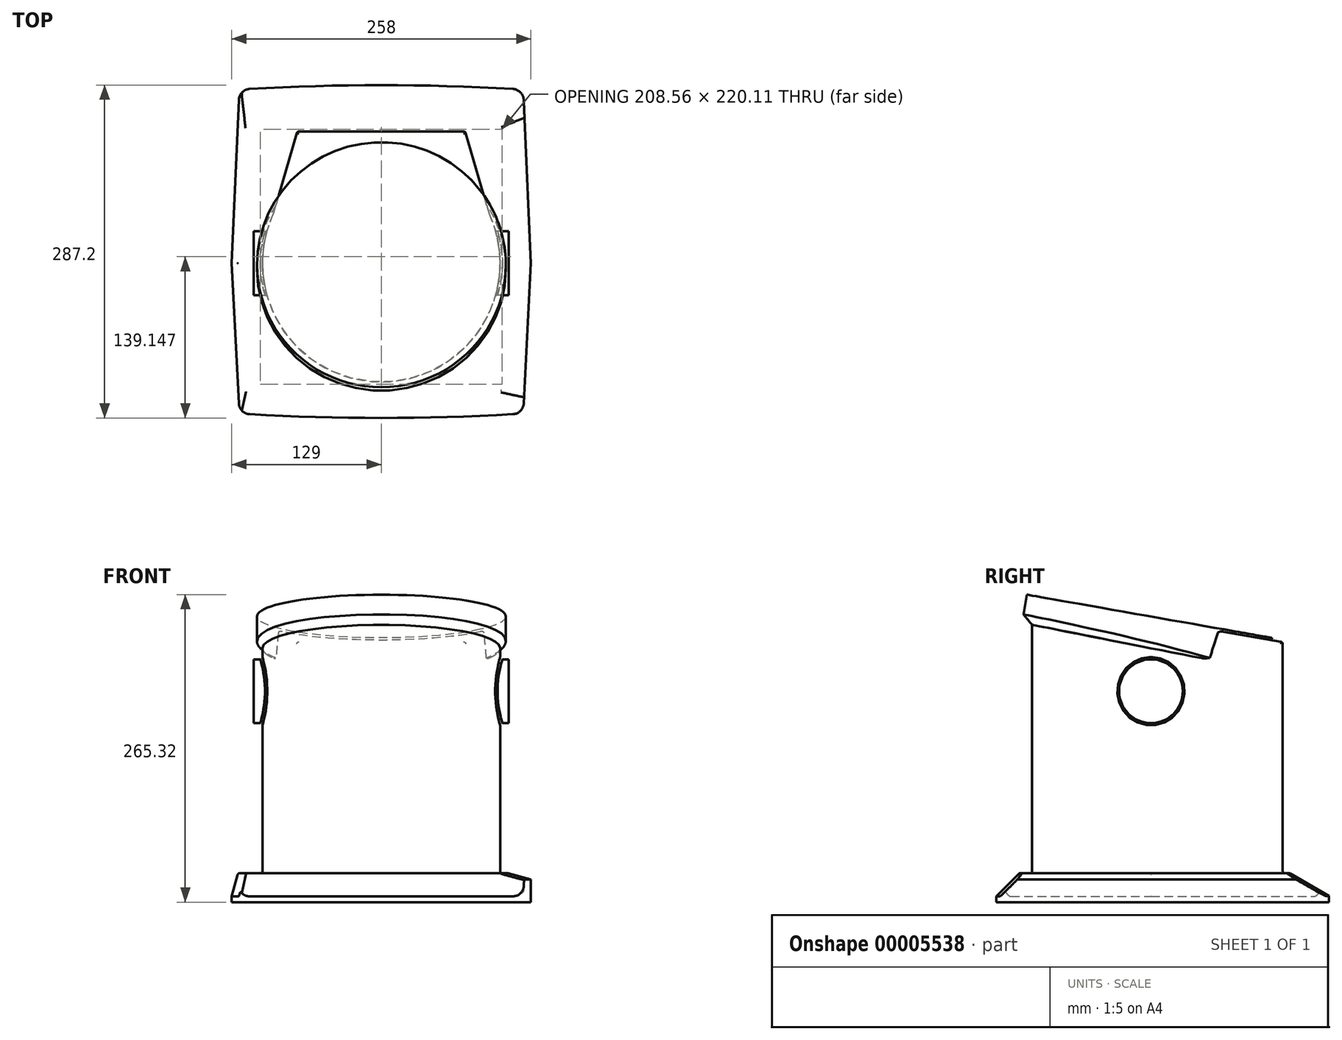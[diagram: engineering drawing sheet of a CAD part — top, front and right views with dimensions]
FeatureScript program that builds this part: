
annotation { "Feature Type Name" : "Feature", "Feature Type Description" : "" }
export const myFeature = defineFeature(function(context is Context, id is Id, definition is map)
    precondition{}
    {
        {
            var Q0;
            Q0=qCreatedBy(makeId("Top.planeOp"),FACE);
            var sketch = newSketch(context, id + "F0", { "sketchPlane" : qUnion([Q0])});
            skLineSegment(sketch, "E0", {"start": v(-129, 0) * mm, "end": v(-122.5, 149.86) * mm});
            skLineSegment(sketch, "E1", {"start": v(-122.5, 149.86) * mm, "end": v(122.5, 149.86) * mm, "construction": true});
            skLineSegment(sketch, "E2", {"start": v(122.5, 149.86) * mm, "end": v(129, 0) * mm});
            skLineSegment(sketch, "E3", {"start": v(129, 0) * mm, "end": v(122.5, -129.84) * mm});
            skLineSegment(sketch, "E4", {"start": v(122.5, -129.84) * mm, "end": v(-122.5, -129.84) * mm, "construction": true});
            skLineSegment(sketch, "E5", {"start": v(-122.5, -129.84) * mm, "end": v(-129, 0) * mm});
            skArc(sketch, "E6", {"start": v(122.5, 149.86) * mm, "mid": v(0, 153.61) * mm, "end": v(-122.5, 149.86) * mm});
            skArc(sketch, "E7", {"start": v(-122.5, -129.84) * mm, "mid": v(0, -133.6) * mm, "end": v(122.5, -129.84) * mm});
            skLineSegment(sketch, "E8", {"start": v(-129, 0) * mm, "end": v(129, 0) * mm, "construction": true});
            skPoint(sketch, "E9", {"position": v(0, 0) * mm});
            skPoint(sketch, "E10", {"position": v(0, 149.86) * mm});
            skPoint(sketch, "E11", {"position": v(0, -129.84) * mm});
            skSolve(sketch);
        }
        {
            var Q0;
            Q0=makeQuery(id+"F0.imprint","IMPRINT",FACE,{"disambiguationData":[TD([[makeQuery(id+"F0.imprint","IMPRINT",EDGE,{"derivedFrom":sQuery(id+"F0.wireOp",EDGE,"E0")}),-1.0]])]});
            extrude(context, id + "F1", {"entities" : qUnion([Q0]), "depth" : 25 * mm});
        }
        {
            var Q0;
            Q0=makeQuery(id+"F1.opExtrude","CAP_EDGE",EDGE,{"disambiguationData":[OSD([sQuery(id+"F0.wireOp",EDGE,"E0")])],"isStart":false});
            var Q1;
            Q1=makeQuery(id+"F1.opExtrude","CAP_EDGE",EDGE,{"disambiguationData":[OSD([sQuery(id+"F0.wireOp",EDGE,"E5")])],"isStart":false});
            var Q2;
            Q2=makeQuery(id+"F1.opExtrude","CAP_EDGE",EDGE,{"disambiguationData":[OSD([sQuery(id+"F0.wireOp",EDGE,"E3")])],"isStart":false});
            var Q3;
            Q3=makeQuery(id+"F1.opExtrude","CAP_EDGE",EDGE,{"disambiguationData":[OSD([sQuery(id+"F0.wireOp",EDGE,"E2")])],"isStart":false});
            chamfer(context, id + "F2", {"entities" : qUnion([Q0, Q1, Q2, Q3]), "chamferType" : ChamferType.OFFSET_ANGLE, "width" : 20 * mm, "oppositeDirection" : false, "angle" : 15 * degree, "tangentPropagation" : true});
        }
        {
            var Q0;
            Q0=makeQuery(id+"F1.opExtrude","CAP_EDGE",EDGE,{"disambiguationData":[OSD([sQuery(id+"F0.wireOp",EDGE,"E7")])],"isStart":false});
            chamfer(context, id + "F3", {"entities" : qUnion([Q0]), "chamferType" : ChamferType.OFFSET_ANGLE, "width" : 20 * mm, "oppositeDirection" : false, "angle" : 45 * degree, "tangentPropagation" : true});
        }
        {
            var Q0;
            Q0=makeQuery(id+"F1.opExtrude","CAP_EDGE",EDGE,{"disambiguationData":[OSD([sQuery(id+"F0.wireOp",EDGE,"E6")])],"isStart":false});
            chamfer(context, id + "F4", {"entities" : qUnion([Q0]), "chamferType" : ChamferType.OFFSET_ANGLE, "width" : 34 * mm, "oppositeDirection" : false, "angle" : 30 * degree, "tangentPropagation" : true});
        }
        {
            var Q0;
            Q0=makeQuery(id+"F1.opExtrude","CAP_FACE",FACE,{"disambiguationData":[OSD([sQuery(id+"F0.wireOp",EDGE,"E0"),sQuery(id+"F0.wireOp",EDGE,"E2"),sQuery(id+"F0.wireOp",EDGE,"E3"),sQuery(id+"F0.wireOp",EDGE,"E5"),sQuery(id+"F0.wireOp",EDGE,"E6"),sQuery(id+"F0.wireOp",EDGE,"E7")])],"isStart":false});
            var sketch = newSketch(context, id + "F5", { "sketchPlane" : qUnion([Q0])});
            skArc(sketch, "E12", {"start": v(-92.81, 43.5) * mm, "mid": v(0, -102.5) * mm, "end": v(92.81, 43.5) * mm});
            skLineSegment(sketch, "E13", {"start": v(-92.81, 43.5) * mm, "end": v(-72.5, 113.61) * mm});
            skLineSegment(sketch, "E14", {"start": v(-72.5, 113.61) * mm, "end": v(72.5, 113.61) * mm});
            skLineSegment(sketch, "E15", {"start": v(72.5, 113.61) * mm, "end": v(92.81, 43.5) * mm});
            skPoint(sketch, "E16", {"position": v(0, 113.61) * mm});
            skSolve(sketch);
        }
        {
            var Q0;
            Q0=makeQuery(id+"F5.imprint","IMPRINT",FACE,{"disambiguationData":[TD([[makeQuery(id+"F5.imprint","IMPRINT",EDGE,{"derivedFrom":sQuery(id+"F5.wireOp",EDGE,"E12")}),1.0]])]});
            extrude(context, id + "F6", {"entities" : qUnion([Q0]), "operationType" : NewBodyOperationType.ADD, "depth" : 240 * mm});
        }
        {
            var Q0;
            Q0=makeQuery(id+"F6.opExtrude","CAP_EDGE",EDGE,{"disambiguationData":[OSD([sQuery(id+"F5.wireOp",EDGE,"E14")])],"isStart":false});
            cPlane(context, id + "F7", {"entities" : qUnion([Q0]), "cplaneType" : CPlaneType.LINE_ANGLE, "offset" : 150 * mm, "angle" : 80 * degree, "width" : 150 * mm, "height" : 150 * mm});
        }
        {
            var Q0;
            Q0=qCreatedBy(id+"F7.planeOp",FACE);
            var sketch = newSketch(context, id + "F8", { "sketchPlane" : qUnion([Q0])});
            skCircle(sketch, "E17", {"center": v(0, -11.31) * mm, "radius": 170.12 * mm});
            skSolve(sketch);
        }
        {
            var Q0;
            Q0=makeQuery(id+"F8.imprint","IMPRINT",FACE,{"disambiguationData":[TD([[makeQuery(id+"F8.imprint","IMPRINT",EDGE,{"derivedFrom":sQuery(id+"F8.wireOp",EDGE,"E17")}),1.0]])]});
            extrude(context, id + "F9", {"entities" : qUnion([Q0]), "operationType" : NewBodyOperationType.REMOVE, "oppositeDirection" : true, "depth" : 40 * mm});
        }
        {
            var Q0;
            Q0=makeQuery(id+"F9.boolean.opBoolean","COPY",FACE,{"derivedFrom":makeQuery(id+"F9.opExtrude","CAP_FACE",FACE,{"disambiguationData":[OSD([sQuery(id+"F8.wireOp",EDGE,"E17")])],"isStart":false})});
            var sketch = newSketch(context, id + "F10", { "sketchPlane" : qUnion([Q0])});
            skCircle(sketch, "E18", {"center": v(0.1, -44.14) * mm, "radius": 102.33 * mm, "construction": true});
            skPoint(sketch, "E18.first.point", {"position": v(-100.45, -63.15) * mm});
            skPoint(sketch, "E18.second.point", {"position": v(21.64, -144.18) * mm});
            skPoint(sketch, "E18.third.point", {"position": v(102.35, -48.13) * mm});
            skCircle(sketch, "E19.0", {"center": v(0.1, -44.14) * mm, "radius": 107.33 * mm});
            skSolve(sketch);
        }
        {
            var Q0;
            Q0=qCreatedBy(makeId("Right.planeOp"),FACE);
            var sketch = newSketch(context, id + "F11", { "sketchPlane" : qUnion([Q0])});
            skCircle(sketch, "E20", {"center": v(0, 182) * mm, "radius": 27.5 * mm});
            skSolve(sketch);
        }
        {
            var Q0;
            Q0=makeQuery(id+"F11.imprint","IMPRINT",FACE,{"disambiguationData":[TD([[makeQuery(id+"F11.imprint","IMPRINT",EDGE,{"derivedFrom":sQuery(id+"F11.wireOp",EDGE,"E20")}),1.0]])]});
            extrude(context, id + "F12", {"entities" : qUnion([Q0]), "operationType" : NewBodyOperationType.ADD, "depth" : 110 * mm});
        }
        {
            var Q0;
            Q0=makeQuery(id+"F11.imprint","IMPRINT",FACE,{"disambiguationData":[TD([[makeQuery(id+"F11.imprint","IMPRINT",EDGE,{"derivedFrom":sQuery(id+"F11.wireOp",EDGE,"E20")}),1.0]])]});
            extrude(context, id + "F13", {"entities" : qUnion([Q0]), "operationType" : NewBodyOperationType.ADD, "oppositeDirection" : true, "depth" : 110 * mm});
        }
        {
            var Q0;
            Q0=makeQuery(id+"F1.opExtrude","CAP_FACE",FACE,{"disambiguationData":[OSD([sQuery(id+"F0.wireOp",EDGE,"E0"),sQuery(id+"F0.wireOp",EDGE,"E2"),sQuery(id+"F0.wireOp",EDGE,"E3"),sQuery(id+"F0.wireOp",EDGE,"E5"),sQuery(id+"F0.wireOp",EDGE,"E6"),sQuery(id+"F0.wireOp",EDGE,"E7")])],"isStart":false});
            var Q1;
            Q1=makeQuery(id+"F6.opExtrude","SWEPT_FACE",FACE,{"disambiguationData":[OSD([sQuery(id+"F5.wireOp",EDGE,"E14")])]});
            var Q2;
            Q2=makeQuery(id+"F6.opExtrude","SWEPT_FACE",FACE,{"disambiguationData":[OSD([sQuery(id+"F5.wireOp",EDGE,"E13")])]});
            var Q3;
            Q3=makeQuery(id+"F6.opExtrude","SWEPT_FACE",FACE,{"disambiguationData":[OSD([sQuery(id+"F5.wireOp",EDGE,"E12")])]});
            var Q4;
            Q4=makeQuery(id+"F9.boolean.opBoolean","COPY",FACE,{"derivedFrom":makeQuery(id+"F9.opExtrude","CAP_FACE",FACE,{"disambiguationData":[OSD([sQuery(id+"F8.wireOp",EDGE,"E17")])],"isStart":false})});
            var Q5;
            Q5=makeQuery(id+"F6.opExtrude","SWEPT_FACE",FACE,{"disambiguationData":[OSD([sQuery(id+"F5.wireOp",EDGE,"E15")])]});
            var Q6;
            Q6=makeQuery(id+"F3.opChamfer","BLEND_EDGE",EDGE,{"blendedFrom":[makeQuery(id+"F1.opExtrude","CAP_EDGE",EDGE,{"disambiguationData":[OSD([sQuery(id+"F0.wireOp",EDGE,"E7")])],"isStart":false}),makeQuery(id+"F2.opChamfer","BLEND_FACE",FACE,{"disambiguationData":[OSD([sQuery(id+"F0.wireOp",EDGE,"E5")])]})],"blendedInto":[makeQuery(id+"F2.opChamfer","BLEND_FACE",FACE,{"disambiguationData":[OSD([sQuery(id+"F0.wireOp",EDGE,"E5")])]})]});
            var Q7;
            Q7=makeQuery(id+"F3.opChamfer","BLEND_EDGE",EDGE,{"blendedFrom":[makeQuery(id+"F1.opExtrude","CAP_EDGE",EDGE,{"disambiguationData":[OSD([sQuery(id+"F0.wireOp",EDGE,"E7")])],"isStart":false}),makeQuery(id+"F2.opChamfer","BLEND_FACE",FACE,{"disambiguationData":[OSD([sQuery(id+"F0.wireOp",EDGE,"E3")])]})],"blendedInto":[makeQuery(id+"F2.opChamfer","BLEND_FACE",FACE,{"disambiguationData":[OSD([sQuery(id+"F0.wireOp",EDGE,"E3")])]})]});
            var Q8;
            Q8=makeQuery(id+"F4.opChamfer","BLEND_EDGE",EDGE,{"blendedFrom":[makeQuery(id+"F1.opExtrude","CAP_EDGE",EDGE,{"disambiguationData":[OSD([sQuery(id+"F0.wireOp",EDGE,"E6")])],"isStart":false}),makeQuery(id+"F2.opChamfer","BLEND_FACE",FACE,{"disambiguationData":[OSD([sQuery(id+"F0.wireOp",EDGE,"E2")])]})],"blendedInto":[makeQuery(id+"F2.opChamfer","BLEND_FACE",FACE,{"disambiguationData":[OSD([sQuery(id+"F0.wireOp",EDGE,"E2")])]})]});
            var Q9;
            Q9=makeQuery(id+"F4.opChamfer","BLEND_EDGE",EDGE,{"blendedFrom":[makeQuery(id+"F1.opExtrude","CAP_EDGE",EDGE,{"disambiguationData":[OSD([sQuery(id+"F0.wireOp",EDGE,"E6")])],"isStart":false}),makeQuery(id+"F2.opChamfer","BLEND_FACE",FACE,{"disambiguationData":[OSD([sQuery(id+"F0.wireOp",EDGE,"E0")])]})],"blendedInto":[makeQuery(id+"F2.opChamfer","BLEND_FACE",FACE,{"disambiguationData":[OSD([sQuery(id+"F0.wireOp",EDGE,"E0")])]})]});
            var Q10;
            Q10=makeQuery(id+"F6.opExtrude","SWEPT_EDGE",EDGE,{"disambiguationData":[OSD([sQuery(id+"F5.wireOp",EDGE,"E12"),sQuery(id+"F5.wireOp",EDGE,"E15")])]});
            var Q11;
            Q11=makeQuery(id+"F2.opChamfer","BLEND_EDGE",EDGE,{"blendedFrom":[makeQuery(id+"F1.opExtrude","CAP_EDGE",EDGE,{"disambiguationData":[OSD([sQuery(id+"F0.wireOp",EDGE,"E2")])],"isStart":false}),makeQuery(id+"F1.opExtrude","CAP_EDGE",EDGE,{"disambiguationData":[OSD([sQuery(id+"F0.wireOp",EDGE,"E3")])],"isStart":false})],"blendedInto":[]});
            var Q12;
            Q12=makeQuery(id+"F1.opExtrude","SWEPT_EDGE",EDGE,{"disambiguationData":[OSD([sQuery(id+"F0.wireOp",EDGE,"E2"),sQuery(id+"F0.wireOp",EDGE,"E3")])]});
            var Q13;
            Q13=makeQuery(id+"F6.opExtrude","SWEPT_EDGE",EDGE,{"disambiguationData":[OSD([sQuery(id+"F5.wireOp",EDGE,"E12"),sQuery(id+"F5.wireOp",EDGE,"E13")])]});
            var Q14;
            Q14=makeQuery(id+"F2.opChamfer","BLEND_EDGE",EDGE,{"blendedFrom":[makeQuery(id+"F1.opExtrude","CAP_EDGE",EDGE,{"disambiguationData":[OSD([sQuery(id+"F0.wireOp",EDGE,"E0")])],"isStart":false}),makeQuery(id+"F1.opExtrude","CAP_EDGE",EDGE,{"disambiguationData":[OSD([sQuery(id+"F0.wireOp",EDGE,"E5")])],"isStart":false})],"blendedInto":[]});
            var Q15;
            Q15=makeQuery(id+"F1.opExtrude","SWEPT_EDGE",EDGE,{"disambiguationData":[OSD([sQuery(id+"F0.wireOp",EDGE,"E0"),sQuery(id+"F0.wireOp",EDGE,"E5")])]});
            fillet(context, id + "F14", {"entities" : qUnion([Q0, Q1, Q2, Q3, Q4, Q5, Q6, Q7, Q8, Q9, Q10, Q11, Q12, Q13, Q14, Q15]), "radius" : 2 * mm, "tangentPropagation" : true, "allowEdgeOverflow" : false});
        }
        {
            var Q0;
            Q0=makeQuery(id+"F1.opExtrude","SWEPT_EDGE",EDGE,{"disambiguationData":[OSD([sQuery(id+"F0.wireOp",EDGE,"E3"),sQuery(id+"F0.wireOp",EDGE,"E7")])]});
            var Q1;
            Q1=makeQuery(id+"F1.opExtrude","SWEPT_EDGE",EDGE,{"disambiguationData":[OSD([sQuery(id+"F0.wireOp",EDGE,"E2"),sQuery(id+"F0.wireOp",EDGE,"E6")])]});
            var Q2;
            Q2=makeQuery(id+"F1.opExtrude","SWEPT_EDGE",EDGE,{"disambiguationData":[OSD([sQuery(id+"F0.wireOp",EDGE,"E0"),sQuery(id+"F0.wireOp",EDGE,"E6")])]});
            var Q3;
            Q3=makeQuery(id+"F1.opExtrude","SWEPT_EDGE",EDGE,{"disambiguationData":[OSD([sQuery(id+"F0.wireOp",EDGE,"E5"),sQuery(id+"F0.wireOp",EDGE,"E7")])]});
            fillet(context, id + "F15", {"entities" : qUnion([Q0, Q1, Q2, Q3]), "radius" : 10 * mm, "tangentPropagation" : true, "allowEdgeOverflow" : false});
        }
        {
            var Q0;
            {var subQ0=makeQuery(id+"F9.opExtrude","CAP_FACE",FACE,{"disambiguationData":[OSD([sQuery(id+"F8.wireOp",EDGE,"E17")])],"isStart":false});var subQ4=makeQuery(id+"F9.boolean.opBoolean","INTERSECT",EDGE,{"derivedFrom":[makeQuery(id+"F6.opExtrude","SWEPT_FACE",FACE,{"disambiguationData":[OSD([sQuery(id+"F5.wireOp",EDGE,"E12")])]}),subQ0]});var subQ9=makeQuery(id+"F10.imprint","IMPRINT",EDGE,{"derivedFrom":subQ4});Q0=qUnion([makeQuery(id+"F10.imprint","IMPRINT",FACE,{"disambiguationData":[TD([[subQ9,-1.0]])]}),makeQuery(id+"F10.imprint","IMPRINT",FACE,{"disambiguationData":[TD([[subQ9,1.0]])]})]);}
            extrude(context, id + "F16", {"entities" : qUnion([Q0]), "operationType" : NewBodyOperationType.ADD, "depth" : 2 * mm});
        }
        {
            var Q0;
            {var subQ0=makeQuery(id+"F9.opExtrude","CAP_FACE",FACE,{"disambiguationData":[OSD([sQuery(id+"F8.wireOp",EDGE,"E17")])],"isStart":false});var subQ4=makeQuery(id+"F9.boolean.opBoolean","INTERSECT",EDGE,{"derivedFrom":[makeQuery(id+"F6.opExtrude","SWEPT_FACE",FACE,{"disambiguationData":[OSD([sQuery(id+"F5.wireOp",EDGE,"E12")])]}),subQ0]});var subQ9=makeQuery(id+"F10.imprint","IMPRINT",EDGE,{"derivedFrom":subQ4});Q0=qUnion([makeQuery(id+"F10.imprint","IMPRINT",FACE,{"disambiguationData":[TD([[subQ9,-1.0]])]}),makeQuery(id+"F10.imprint","IMPRINT",FACE,{"disambiguationData":[TD([[subQ9,1.0]])]})]);}
            extrude(context, id + "F17", {"entities" : qUnion([Q0]), "operationType" : NewBodyOperationType.ADD, "oppositeDirection" : true, "depth" : 13 * mm});
        }
        {
            var Q0;
            Q0=makeQuery(id+"F17.boolean.opBoolean","INTERSECT",EDGE,{"derivedFrom":[makeQuery(id+"F6.opExtrude","SWEPT_FACE",FACE,{"disambiguationData":[OSD([sQuery(id+"F5.wireOp",EDGE,"E12")])]}),makeQuery(id+"F17.opExtrude","CAP_FACE",FACE,{"disambiguationData":[OSD([sQuery(id+"F10.wireOp",EDGE,"E19.0")])],"isStart":false})]});
            chamfer(context, id + "F18", {"entities" : qUnion([Q0]), "width" : 10 * mm});
        }
        {
            var Q0;
            Q0=makeQuery(id+"F1.opExtrude","SWEPT_BODY",BODY,{"disambiguationData":[OSD([sQuery(id+"F0.wireOp",EDGE,"E0"),sQuery(id+"F0.wireOp",EDGE,"E2"),sQuery(id+"F0.wireOp",EDGE,"E3"),sQuery(id+"F0.wireOp",EDGE,"E5"),sQuery(id+"F0.wireOp",EDGE,"E6"),sQuery(id+"F0.wireOp",EDGE,"E7")])]});
            transform(context, id + "F19", {"entities" : qUnion([Q0]), "transformType" : TransformType.TRANSLATION_3D, "dx" : 0 * mm, "dy" : 0 * mm, "dz" : 0 * mm, "makeCopy" : true});
        }
    });
